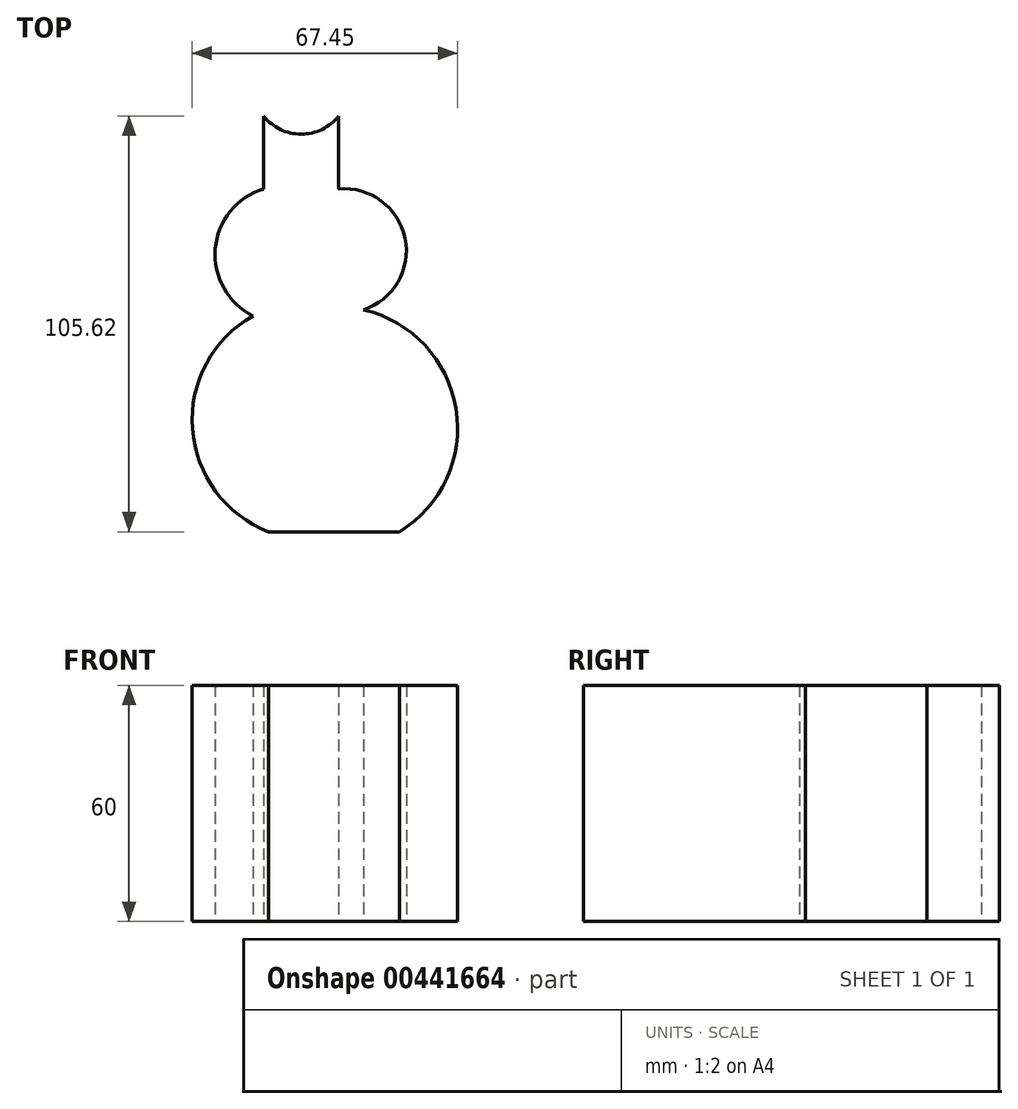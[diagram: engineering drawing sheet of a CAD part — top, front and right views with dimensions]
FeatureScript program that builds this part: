
annotation { "Feature Type Name" : "Feature", "Feature Type Description" : "" }
export const myFeature = defineFeature(function(context is Context, id is Id, definition is map)
    precondition{}
    {
        {
            var Q0;
            Q0=qCreatedBy(makeId("Top.planeOp"),FACE);
            var sketch = newSketch(context, id + "F0", { "sketchPlane" : qUnion([Q0])});
            skLineSegment(sketch, "E0", {"start": v(23.16, -41.3) * mm, "end": v(0, -41.3) * mm});
            skLineSegment(sketch, "E1", {"start": v(0, -41.3) * mm, "end": v(-10.06, -41.3) * mm});
            skArc(sketch, "E2", {"start": v(-14.02, 13.56) * mm, "mid": v(-29.43, -15.12) * mm, "end": v(-10.06, -41.3) * mm});
            skArc(sketch, "E3", {"start": v(23.16, -41.3) * mm, "mid": v(37.54, -10.03) * mm, "end": v(14.02, 15.09) * mm});
            skArc(sketch, "E4", {"start": v(-11.33, 45.83) * mm, "mid": v(-23.64, 30.6) * mm, "end": v(-14.02, 13.56) * mm});
            skLineSegment(sketch, "E5", {"start": v(-11.33, 45.83) * mm, "end": v(-11.33, 64.32) * mm});
            skLineSegment(sketch, "E6", {"start": v(7.72, 64.32) * mm, "end": v(7.72, 45.83) * mm});
            skArc(sketch, "E7", {"start": v(14.02, 15.09) * mm, "mid": v(24.58, 33.27) * mm, "end": v(7.72, 45.83) * mm});
            skArc(sketch, "E8", {"start": v(7.72, 64.32) * mm, "mid": v(-1.8, 68.42) * mm, "end": v(-11.33, 64.32) * mm});
            skArc(sketch, "E9", {"start": v(-11.33, 64.32) * mm, "mid": v(-1.8, 59.74) * mm, "end": v(7.72, 64.32) * mm});
            skSolve(sketch);
        }
        {
            var Q0;
            Q0=makeQuery(id+"F0.imprint","IMPRINT",FACE,{"disambiguationData":[TD([[makeQuery(id+"F0.imprint","IMPRINT",EDGE,{"derivedFrom":sQuery(id+"F0.wireOp",EDGE,"E0")}),-1.0]])]});
            extrude(context, id + "F1", {"entities" : qUnion([Q0]), "depth" : 60 * mm});
        }
    });
